# Revit family: E2SPH_2014
name_source: partatom
category: Specialty Equipment
revit_build: Autodesk Revit 2014 (Build: 20130308_1515(x64)
units: mm (PartAtom-declared; Revit-internal decimal feet)

## types (1)
- 4'-0" Length
    Bumper = Extruded PVC - 701 Black
    Case = Textured Sheet Metal (Steel Painted) - 701 Black
    Case Interior - Back Panel = Sheet Metal (Steel Painted) - 701 Black
    Case Interior - Side Panel = Mirror
    Case Weight = 700.00 lbf
    Cutsheet URL = http://www.hussmann.com
    Depth = 63"
    Description = Self-Service Multi-Deck Display With Prep Top and Hot Wells
    Door Frame = Plastic - 701 Black
    End Weight = 75.00 lbf
    Ends = Textured Sheet Metal (Steel Painted) - 701 Black
    Glazing = Glass
    Height = 53 3/4"
    Manufacturer = Hussmann Corporation
    Manufacturer Disclaimer = The information in this file is not intended to be an exact representation of the corresponding Hussmann product.  Further, we reserve the right to change or revise specifications and product design in connection with any feature of our products. Such changes do not entitle the buyer to corresponding changes, improvements, additions, or replacements for equipment previously sold or shipped.
    Model = E2SPH
    Model URL = http://www.hussmann.com
    Note from Manufacturer = This model only comes in 4'-0" length.
    Number of Shelves = 2
    Number of Supports = 2
    Refrig. Liquid = Liquid
    Refrig. Suction = Suction
    Refrigeration Lines Liquid = 3/8"
    Refrigeration Lines Suction = 7/8"
    Revit Family Date = 05/26/2016
    Shelves = Sheet Metal (Steel Painted) - 701 Black
    Splashguard = Textured Sheet Metal (Steel Painted) - 701 Black
    Total Weight = 850.00 lbf
    Trim = Stainless Steel
    Type Comments = Elite
    URL = www.hussmann.com
    Waste Drain = 1 1/2"
    Waste Drain Location = 24"
    Width = 48 1/8"

## geometry (parser evidence)
native form markers: Sweep x6
no freeform markers — native parametric forms only
